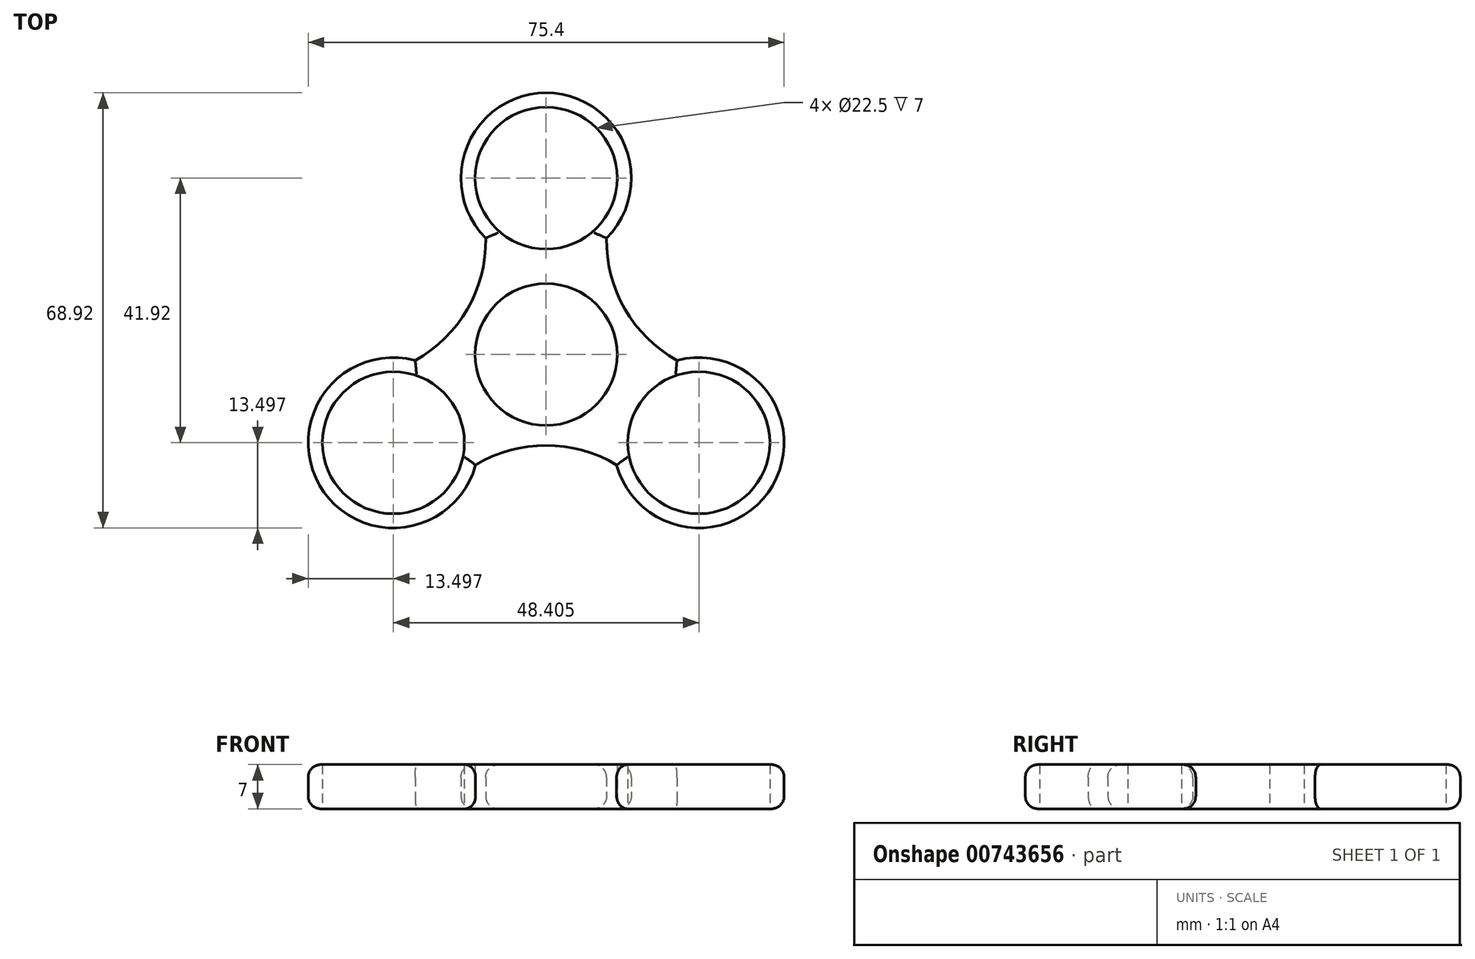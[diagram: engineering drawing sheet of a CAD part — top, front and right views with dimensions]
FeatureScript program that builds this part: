
annotation { "Feature Type Name" : "Feature", "Feature Type Description" : "" }
export const myFeature = defineFeature(function(context is Context, id is Id, definition is map)
    precondition{}
    {
        {
            var Q0;
            Q0=qCreatedBy(makeId("Top.planeOp"),FACE);
            var sketch = newSketch(context, id + "F0", { "sketchPlane" : qUnion([Q0])});
            skCircle(sketch, "E0", {"center": v(0, 0) * mm, "radius": 11.25 * mm});
            skCircle(sketch, "E1", {"center": v(0, 27.95) * mm, "radius": 11.25 * mm});
            skCircle(sketch, "E2.1.0", {"center": v(-24.2, -13.97) * mm, "radius": 11.25 * mm});
            skCircle(sketch, "E2.2.0", {"center": v(24.2, -13.97) * mm, "radius": 11.25 * mm});
            skArc(sketch, "E3", {"start": v(9.58, 18.43) * mm, "mid": v(0, 41.45) * mm, "end": v(-9.58, 18.43) * mm});
            skArc(sketch, "E4.1.0", {"start": v(-20.75, -0.92) * mm, "mid": v(-35.9, -20.72) * mm, "end": v(-11.17, -17.51) * mm});
            skArc(sketch, "E4.2.0", {"start": v(11.17, -17.51) * mm, "mid": v(35.9, -20.72) * mm, "end": v(20.75, -0.92) * mm});
            skArc(sketch, "E5.trimOffspring", {"start": v(9.58, 18.43) * mm, "mid": v(12.47, 7.2) * mm, "end": v(20.75, -0.92) * mm});
            skArc(sketch, "E6.trimOffspring", {"start": v(11.17, -17.51) * mm, "mid": v(0, -14.4) * mm, "end": v(-11.17, -17.51) * mm});
            skArc(sketch, "E7.trimOffspring", {"start": v(-20.75, -0.92) * mm, "mid": v(-12.47, 7.2) * mm, "end": v(-9.58, 18.43) * mm});
            skSolve(sketch);
        }
        {
            var Q0;
            Q0 = qSketchRegion(id + "F0", true);
            extrude(context, id + "F1", {"entities" : qUnion([Q0]), "depth" : 7 * mm, "offsetDistance" : 25 * mm});
        }
        {
            var Q0;
            Q0=makeQuery(id+"F1.opExtrude","CAP_EDGE",EDGE,{"disambiguationData":[OSD([sQuery(id+"F0.wireOp",EDGE,"E3")])],"isStart":false});
            var Q1;
            Q1=makeQuery(id+"F1.opExtrude","CAP_EDGE",EDGE,{"disambiguationData":[OSD([sQuery(id+"F0.wireOp",EDGE,"E7.trimOffspring")])],"isStart":false});
            var Q2;
            Q2=makeQuery(id+"F1.opExtrude","CAP_EDGE",EDGE,{"disambiguationData":[OSD([sQuery(id+"F0.wireOp",EDGE,"E4.1.0")])],"isStart":false});
            var Q3;
            Q3=makeQuery(id+"F1.opExtrude","CAP_EDGE",EDGE,{"disambiguationData":[OSD([sQuery(id+"F0.wireOp",EDGE,"E6.trimOffspring")])],"isStart":false});
            var Q4;
            Q4=makeQuery(id+"F1.opExtrude","CAP_EDGE",EDGE,{"disambiguationData":[OSD([sQuery(id+"F0.wireOp",EDGE,"E4.2.0")])],"isStart":false});
            var Q5;
            Q5=makeQuery(id+"F1.opExtrude","CAP_EDGE",EDGE,{"disambiguationData":[OSD([sQuery(id+"F0.wireOp",EDGE,"E5.trimOffspring")])],"isStart":false});
            var Q6;
            Q6=makeQuery(id+"F1.opExtrude","CAP_EDGE",EDGE,{"disambiguationData":[OSD([sQuery(id+"F0.wireOp",EDGE,"E7.trimOffspring")])],"isStart":true});
            var Q7;
            Q7=makeQuery(id+"F1.opExtrude","CAP_EDGE",EDGE,{"disambiguationData":[OSD([sQuery(id+"F0.wireOp",EDGE,"E3")])],"isStart":true});
            var Q8;
            Q8=makeQuery(id+"F1.opExtrude","CAP_EDGE",EDGE,{"disambiguationData":[OSD([sQuery(id+"F0.wireOp",EDGE,"E5.trimOffspring")])],"isStart":true});
            var Q9;
            Q9=makeQuery(id+"F1.opExtrude","CAP_EDGE",EDGE,{"disambiguationData":[OSD([sQuery(id+"F0.wireOp",EDGE,"E4.2.0")])],"isStart":true});
            var Q10;
            Q10=makeQuery(id+"F1.opExtrude","CAP_EDGE",EDGE,{"disambiguationData":[OSD([sQuery(id+"F0.wireOp",EDGE,"E6.trimOffspring")])],"isStart":true});
            var Q11;
            Q11=makeQuery(id+"F1.opExtrude","CAP_EDGE",EDGE,{"disambiguationData":[OSD([sQuery(id+"F0.wireOp",EDGE,"E4.1.0")])],"isStart":true});
            fillet(context, id + "F2", {"entities" : qUnion([Q0, Q1, Q2, Q3, Q4, Q5, Q6, Q7, Q8, Q9, Q10, Q11]), "radius" : 2 * mm, "tangentPropagation" : true, "allowEdgeOverflow" : false});
        }
    });
